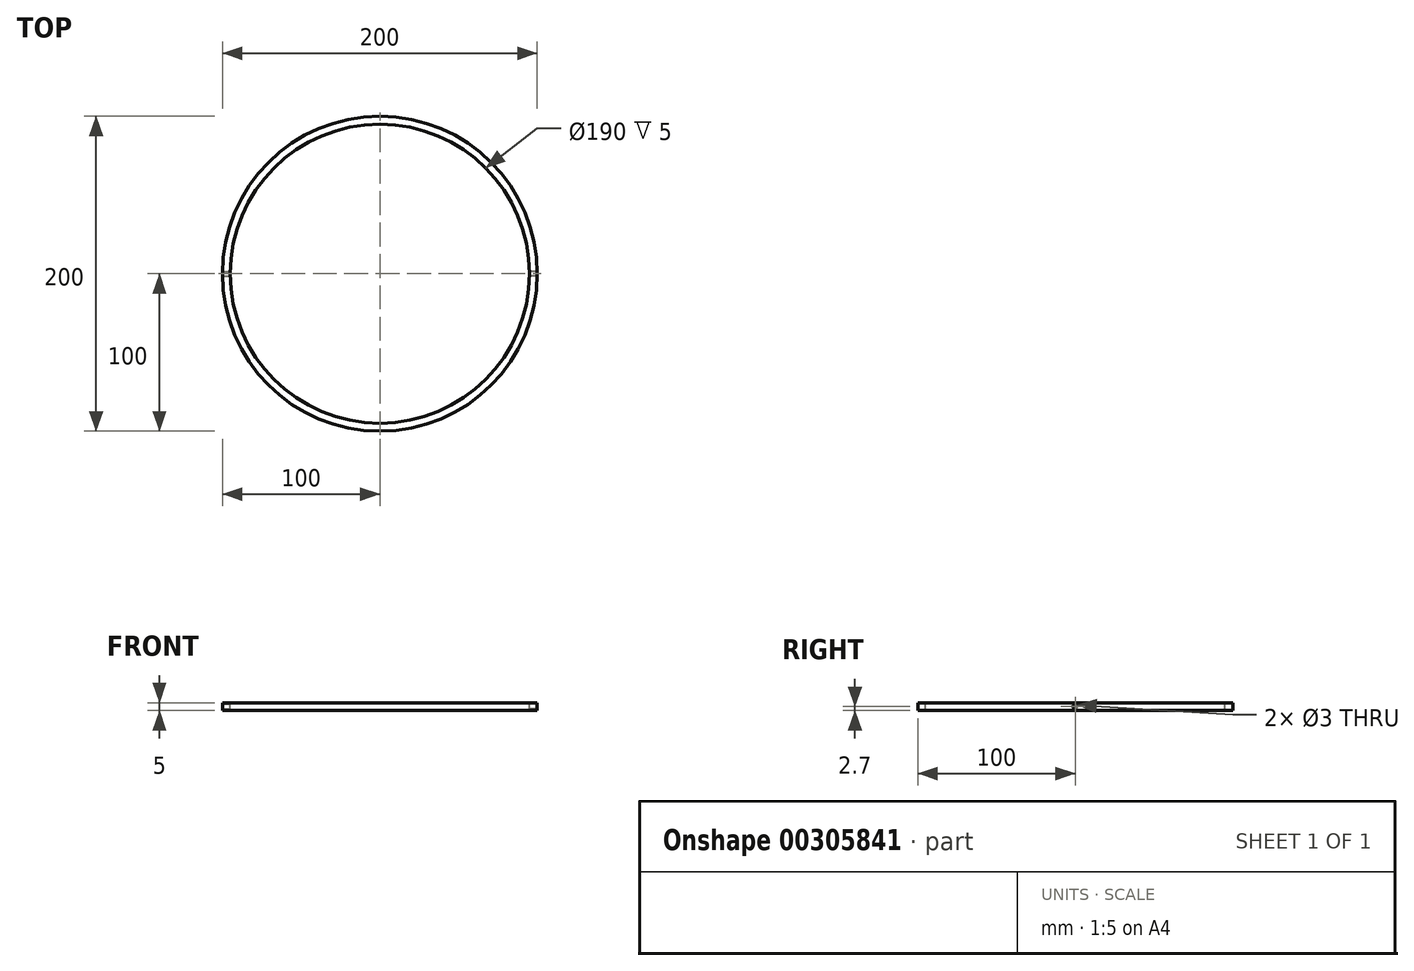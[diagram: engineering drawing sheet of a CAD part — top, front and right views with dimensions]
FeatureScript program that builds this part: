
annotation { "Feature Type Name" : "Feature", "Feature Type Description" : "" }
export const myFeature = defineFeature(function(context is Context, id is Id, definition is map)
    precondition{}
    {
        {
            var Q0;
            Q0=qCreatedBy(makeId("Right.planeOp"),FACE);
            var sketch = newSketch(context, id + "F0", { "sketchPlane" : qUnion([Q0])});
            skLineSegment(sketch, "E0", {"start": v(0, 2.5) * mm, "end": v(0, 0) * mm});
            skLineSegment(sketch, "E1.bottom", {"start": v(-100, 4.8) * mm, "end": v(-95, 4.8) * mm});
            skLineSegment(sketch, "E1.top", {"start": v(-100, -0.2) * mm, "end": v(-95, -0.2) * mm});
            skLineSegment(sketch, "E1.left", {"start": v(-100, 4.8) * mm, "end": v(-100, -0.2) * mm});
            skLineSegment(sketch, "E1.right", {"start": v(-95, 4.8) * mm, "end": v(-95, -0.2) * mm});
            skPoint(sketch, "E2", {"position": v(0, 2.5) * mm});
            skPoint(sketch, "E3", {"position": v(-95, 2.3) * mm});
            skPoint(sketch, "E4", {"position": v(-100, -0.2) * mm});
            skPoint(sketch, "E5", {"position": v(-100, 2.3) * mm});
            skSolve(sketch);
        }
        {
            var Q0;
            Q0=makeQuery(id+"F0.imprint","IMPRINT",FACE,{"disambiguationData":[TD([[makeQuery(id+"F0.imprint","IMPRINT",EDGE,{"derivedFrom":sQuery(id+"F0.wireOp",EDGE,"E1.bottom")}),-1.0]])]});
            var Q1;
            Q1=sQuery(id+"F0.wireOp",EDGE,"E0");
            revolve(context, id + "F1", {"entities" : qUnion([Q0]), "axis" : qUnion([Q1]), "revolveType" : RevolveType.FULL});
        }
        {
            var Q0;
            Q0=sQuery(id+"F0.wireOp",VERTEX,"E2");
            var Q1;
            Q1=makeQuery(id+"F1.opRevolve","SWEPT_BODY",BODY,{"disambiguationData":[OSD([sQuery(id+"F0.wireOp",EDGE,"E1.bottom"),sQuery(id+"F0.wireOp",EDGE,"E1.top"),sQuery(id+"F0.wireOp",EDGE,"E1.left"),sQuery(id+"F0.wireOp",EDGE,"E1.right")])]});
            hole(context, id + "F2", {"style" : HoleStyle.SIMPLE, "endStyle" : HoleEndStyle.THROUGH, "holeDiameter" : 3 * mm, "tappedDepth" : 12 * mm, "tapClearance" : 3, "locations" : qUnion([Q0]), "scope" : qUnion([Q1])});
        }
        {
            var Q0;
            Q0=sQuery(id+"F0.wireOp",VERTEX,"E2");
            var Q1;
            Q1=makeQuery(id+"F1.opRevolve","SWEPT_BODY",BODY,{"disambiguationData":[OSD([sQuery(id+"F0.wireOp",EDGE,"E1.bottom"),sQuery(id+"F0.wireOp",EDGE,"E1.top"),sQuery(id+"F0.wireOp",EDGE,"E1.left"),sQuery(id+"F0.wireOp",EDGE,"E1.right")])]});
            hole(context, id + "F3", {"style" : HoleStyle.SIMPLE, "endStyle" : HoleEndStyle.THROUGH, "oppositeDirection" : true, "holeDiameter" : 3 * mm, "tappedDepth" : 12 * mm, "tapClearance" : 3, "locations" : qUnion([Q0]), "scope" : qUnion([Q1])});
        }
    });
